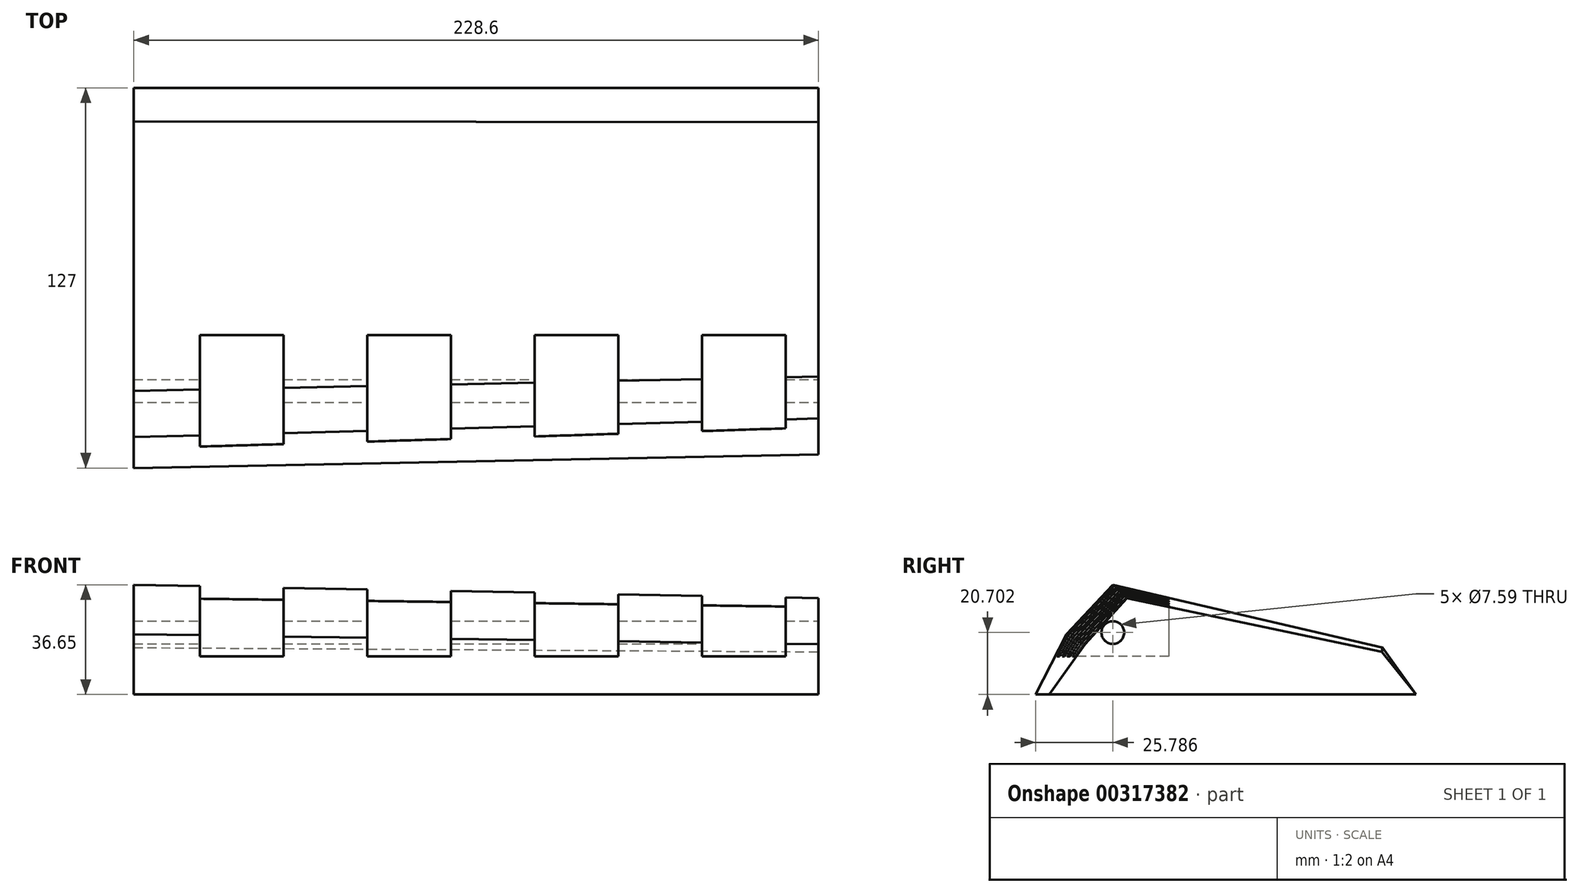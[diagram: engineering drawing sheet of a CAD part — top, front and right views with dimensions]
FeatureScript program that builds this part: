
annotation { "Feature Type Name" : "Feature", "Feature Type Description" : "" }
export const myFeature = defineFeature(function(context is Context, id is Id, definition is map)
    precondition{}
    {
        {
            var Q0;
            Q0=qCreatedBy(makeId("Right.planeOp"),FACE);
            var sketch = newSketch(context, id + "F0", { "sketchPlane" : qUnion([Q0])});
            skLineSegment(sketch, "E0", {"start": v(0, 0) * mm, "end": v(-127, 0) * mm});
            skLineSegment(sketch, "E1", {"start": v(-127, 0) * mm, "end": v(-116.66, 20.14) * mm});
            skLineSegment(sketch, "E2", {"start": v(-116.66, 20.14) * mm, "end": v(-101.27, 36.65) * mm});
            skLineSegment(sketch, "E3", {"start": v(-101.27, 36.65) * mm, "end": v(-11.2, 15.67) * mm});
            skLineSegment(sketch, "E4", {"start": v(-11.2, 15.67) * mm, "end": v(0, 0) * mm});
            skSolve(sketch);
        }
        {
            var Q0;
            Q0=qCreatedBy(makeId("Right.planeOp"),FACE);
            cPlane(context, id + "F1", {"entities" : qUnion([Q0]), "cplaneType" : CPlaneType.OFFSET, "offset" : 228.6 * mm, "width" : 152.4 * mm, "height" : 152.4 * mm});
        }
        {
            var Q0;
            Q0=qCreatedBy(id+"F1.planeOp",FACE);
            var sketch = newSketch(context, id + "F2", { "sketchPlane" : qUnion([Q0])});
            skLineSegment(sketch, "E5", {"start": v(0, 0) * mm, "end": v(-122.48, 0) * mm});
            skLineSegment(sketch, "E6", {"start": v(-122.48, 0) * mm, "end": v(-110.45, 16.79) * mm});
            skLineSegment(sketch, "E7", {"start": v(-110.45, 16.79) * mm, "end": v(-96.46, 32.17) * mm});
            skLineSegment(sketch, "E8", {"start": v(-96.46, 32.17) * mm, "end": v(-11.41, 14.27) * mm});
            skLineSegment(sketch, "E9", {"start": v(-11.41, 14.27) * mm, "end": v(0, 0) * mm});
            skSolve(sketch);
        }
        {
            var Q0;
            Q0=makeQuery(id+"F0.imprint","IMPRINT",FACE,{"disambiguationData":[TD([[makeQuery(id+"F0.imprint","IMPRINT",EDGE,{"derivedFrom":sQuery(id+"F0.wireOp",EDGE,"E0")}),-1.0]])]});
            var Q1;
            Q1=makeQuery(id+"F2.imprint","IMPRINT",FACE,{"disambiguationData":[TD([[makeQuery(id+"F2.imprint","IMPRINT",EDGE,{"derivedFrom":sQuery(id+"F2.wireOp",EDGE,"E5")}),-1.0]])]});
            loft(context, id + "F3", {"sheetProfilesArray" : [{ "sheetProfileEntities" : qUnion([Q0]) }, { "sheetProfileEntities" : qUnion([Q1]) }]});
        }
        {
            var Q0;
            Q0=qCreatedBy(id+"F1.planeOp",FACE);
            var sketch = newSketch(context, id + "F4", { "sketchPlane" : qUnion([Q0])});
            skLineSegment(sketch, "E10", {"start": v(0, 0) * mm, "end": v(-101.21, 0) * mm, "construction": true});
            skLineSegment(sketch, "E11", {"start": v(-101.21, 0) * mm, "end": v(-101.21, 20.7) * mm, "construction": true});
            skCircle(sketch, "E12", {"center": v(-101.21, 20.7) * mm, "radius": 3.8 * mm});
            skLineSegment(sketch, "E13", {"start": v(-105.01, 20.7) * mm, "end": v(-105.01, 0) * mm, "construction": true});
            skLineSegment(sketch, "E14", {"start": v(-97.42, 20.7) * mm, "end": v(-97.42, 0) * mm});
            skSolve(sketch);
        }
        {
            var Q0;
            Q0=makeQuery(id+"F4.imprint","IMPRINT",FACE,{"disambiguationData":[TD([[makeQuery(id+"F4.imprint","IMPRINT",EDGE,{"derivedFrom":sQuery(id+"F4.wireOp",EDGE,"E12")}),1.0]])]});
            extrude(context, id + "F5", {"entities" : qUnion([Q0]), "operationType" : NewBodyOperationType.REMOVE, "oppositeDirection" : true, "depth" : 228.6 * mm});
        }
        {
            var Q0;
            Q0=qCreatedBy(makeId("Top.planeOp"),FACE);
            cPlane(context, id + "F6", {"entities" : qUnion([Q0]), "cplaneType" : CPlaneType.OFFSET, "offset" : 16.92 * mm, "width" : 152.4 * mm, "height" : 152.4 * mm});
        }
        {
            var Q0;
            Q0=qCreatedBy(id+"F6.planeOp",FACE);
            var sketch = newSketch(context, id + "F7", { "sketchPlane" : qUnion([Q0])});
            skLineSegment(sketch, "E15", {"start": v(0, 0) * mm, "end": v(36.07, 0) * mm, "construction": true});
            skLineSegment(sketch, "E16", {"start": v(36.07, 0) * mm, "end": v(91.95, 0) * mm, "construction": true});
            skLineSegment(sketch, "E17", {"start": v(91.95, 0) * mm, "end": v(147.83, 0) * mm, "construction": true});
            skLineSegment(sketch, "E18", {"start": v(147.83, 0) * mm, "end": v(203.7, 0) * mm, "construction": true});
            skLineSegment(sketch, "E19", {"start": v(203.7, 0) * mm, "end": v(203.7, -96.52) * mm});
            skLineSegment(sketch, "E20", {"start": v(203.7, 0) * mm, "end": v(203.7, -106.68) * mm});
            skLineSegment(sketch, "E21", {"start": v(203.7, -96.52) * mm, "end": v(147.83, -96.52) * mm, "construction": true});
            skLineSegment(sketch, "E22", {"start": v(147.83, -96.52) * mm, "end": v(91.95, -96.52) * mm, "construction": true});
            skLineSegment(sketch, "E23", {"start": v(91.95, -96.52) * mm, "end": v(36.07, -96.52) * mm, "construction": true});
            skLineSegment(sketch, "E24", {"start": v(36.07, -96.52) * mm, "end": v(0, -96.52) * mm, "construction": true});
            skLineSegment(sketch, "E25.bottom", {"start": v(50.04, -82.55) * mm, "end": v(22.1, -82.55) * mm});
            skLineSegment(sketch, "E25.top", {"start": v(50.04, -110.49) * mm, "end": v(22.1, -110.49) * mm});
            skLineSegment(sketch, "E25.left", {"start": v(50.04, -82.55) * mm, "end": v(50.04, -110.49) * mm});
            skLineSegment(sketch, "E25.right", {"start": v(22.1, -82.55) * mm, "end": v(22.1, -110.49) * mm});
            skPoint(sketch, "E25.middle", {"position": v(36.07, -96.52) * mm});
            skLineSegment(sketch, "E26.bottom", {"start": v(105.92, -82.55) * mm, "end": v(77.98, -82.55) * mm});
            skLineSegment(sketch, "E26.top", {"start": v(105.92, -110.5) * mm, "end": v(77.98, -110.5) * mm});
            skLineSegment(sketch, "E26.left", {"start": v(105.92, -82.55) * mm, "end": v(105.92, -110.5) * mm});
            skLineSegment(sketch, "E26.right", {"start": v(77.98, -82.55) * mm, "end": v(77.98, -110.5) * mm});
            skPoint(sketch, "E26.middle", {"position": v(91.95, -96.52) * mm});
            skLineSegment(sketch, "E27.bottom", {"start": v(161.8, -82.55) * mm, "end": v(133.86, -82.55) * mm});
            skLineSegment(sketch, "E27.top", {"start": v(161.8, -110.5) * mm, "end": v(133.86, -110.5) * mm});
            skLineSegment(sketch, "E27.left", {"start": v(161.8, -82.55) * mm, "end": v(161.8, -110.5) * mm});
            skLineSegment(sketch, "E27.right", {"start": v(133.86, -82.55) * mm, "end": v(133.86, -110.5) * mm});
            skPoint(sketch, "E27.middle", {"position": v(147.83, -96.52) * mm});
            skLineSegment(sketch, "E28.bottom", {"start": v(189.74, -82.55) * mm, "end": v(217.68, -82.55) * mm});
            skLineSegment(sketch, "E28.top", {"start": v(189.74, -110.5) * mm, "end": v(217.68, -110.5) * mm});
            skLineSegment(sketch, "E28.left", {"start": v(189.74, -82.55) * mm, "end": v(189.74, -110.5) * mm});
            skLineSegment(sketch, "E28.right", {"start": v(217.68, -82.55) * mm, "end": v(217.68, -110.5) * mm});
            skPoint(sketch, "E28.middle", {"position": v(203.7, -96.52) * mm});
            skPoint(sketch, "E28.cornerSnap0", {"position": v(91.95, -82.55) * mm});
            skSolve(sketch);
        }
        {
            var Q0;
            Q0 = qSketchRegion(id + "F7", true);
            extrude(context, id + "F8", {"entities" : qUnion([Q0]), "operationType" : NewBodyOperationType.REMOVE, "depth" : 25.4 * mm});
        }
        {
            var Q0;
            Q0=makeQuery(id+"F8.boolean.opBoolean","COPY",FACE,{"derivedFrom":makeQuery(id+"F8.opExtrude","SWEPT_FACE",FACE,{"disambiguationData":[OSD([sQuery(id+"F7.wireOp",EDGE,"E25.bottom")])]})});
            var sketch = newSketch(context, id + "F9", { "sketchPlane" : qUnion([Q0])});
            skLineSegment(sketch, "E29", {"start": v(22.1, 32) * mm, "end": v(22.1, 16.92) * mm});
            skLineSegment(sketch, "E30", {"start": v(22.1, 16.92) * mm, "end": v(50.04, 16.92) * mm});
            skLineSegment(sketch, "E31", {"start": v(50.04, 16.92) * mm, "end": v(50.04, 31.64) * mm});
            skLineSegment(sketch, "E32", {"start": v(50.04, 31.64) * mm, "end": v(22.1, 32) * mm});
            skSolve(sketch);
        }
        {
            var Q0;
            Q0=makeQuery(id+"F8.boolean.opBoolean","COPY",FACE,{"derivedFrom":makeQuery(id+"F8.opExtrude","SWEPT_FACE",FACE,{"disambiguationData":[OSD([sQuery(id+"F7.wireOp",EDGE,"E26.bottom")])]})});
            var sketch = newSketch(context, id + "F10", { "sketchPlane" : qUnion([Q0])});
            skLineSegment(sketch, "E33", {"start": v(77.98, 31.27) * mm, "end": v(77.98, 16.92) * mm});
            skLineSegment(sketch, "E34", {"start": v(77.98, 16.92) * mm, "end": v(105.92, 16.92) * mm});
            skLineSegment(sketch, "E35", {"start": v(105.92, 16.92) * mm, "end": v(105.92, 30.9) * mm});
            skLineSegment(sketch, "E36", {"start": v(105.92, 30.9) * mm, "end": v(77.98, 31.27) * mm});
            skSolve(sketch);
        }
        {
            var Q0;
            Q0=makeQuery(id+"F8.boolean.opBoolean","COPY",FACE,{"derivedFrom":makeQuery(id+"F8.opExtrude","SWEPT_FACE",FACE,{"disambiguationData":[OSD([sQuery(id+"F7.wireOp",EDGE,"E27.bottom")])]})});
            var sketch = newSketch(context, id + "F11", { "sketchPlane" : qUnion([Q0])});
            skLineSegment(sketch, "E37", {"start": v(133.86, 30.53) * mm, "end": v(133.86, 16.92) * mm});
            skLineSegment(sketch, "E38", {"start": v(133.86, 16.92) * mm, "end": v(161.8, 16.92) * mm});
            skLineSegment(sketch, "E39", {"start": v(161.8, 16.92) * mm, "end": v(161.8, 30.15) * mm});
            skLineSegment(sketch, "E40", {"start": v(161.8, 30.15) * mm, "end": v(133.86, 30.53) * mm});
            skSolve(sketch);
        }
        {
            var Q0;
            Q0=makeQuery(id+"F8.boolean.opBoolean","COPY",FACE,{"derivedFrom":makeQuery(id+"F8.opExtrude","SWEPT_FACE",FACE,{"disambiguationData":[OSD([sQuery(id+"F7.wireOp",EDGE,"E28.bottom")])]})});
            var sketch = newSketch(context, id + "F12", { "sketchPlane" : qUnion([Q0])});
            skLineSegment(sketch, "E41", {"start": v(189.74, 29.77) * mm, "end": v(189.74, 16.92) * mm});
            skLineSegment(sketch, "E42", {"start": v(189.74, 16.92) * mm, "end": v(217.68, 16.92) * mm});
            skLineSegment(sketch, "E43", {"start": v(217.68, 16.92) * mm, "end": v(217.68, 29.4) * mm});
            skLineSegment(sketch, "E44", {"start": v(217.68, 29.4) * mm, "end": v(189.74, 29.77) * mm});
            skSolve(sketch);
        }
        {
            var Q0;
            Q0 = qSketchRegion(id + "F9", true);
            var Q1;
            Q1 = qSketchRegion(id + "F10", true);
            var Q2;
            Q2 = qSketchRegion(id + "F11", true);
            var Q3;
            Q3 = qSketchRegion(id + "F12", true);
            extrude(context, id + "F13", {"entities" : qUnion([Q0, Q1, Q2, Q3]), "operationType" : NewBodyOperationType.REMOVE, "depth" : 609.6 * mm});
        }
        {
            var Q0;
            Q0=qCreatedBy(makeId("Top.planeOp"),FACE);
            cPlane(context, id + "F14", {"entities" : qUnion([Q0]), "cplaneType" : CPlaneType.OFFSET, "offset" : 12.7 * mm, "width" : 152.4 * mm, "height" : 152.4 * mm});
        }
        {
            var Q0;
            Q0=qCreatedBy(id+"F14.planeOp",FACE);
            var sketch = newSketch(context, id + "F15", { "sketchPlane" : qUnion([Q0])});
            skLineSegment(sketch, "E45", {"start": v(0, 0) * mm, "end": v(36.07, 0) * mm, "construction": true});
            skLineSegment(sketch, "E46", {"start": v(36.07, 0) * mm, "end": v(91.95, 0) * mm, "construction": true});
            skPoint(sketch, "E46.endSnap0", {"position": v(18.03, 0) * mm});
            skLineSegment(sketch, "E47", {"start": v(91.95, 0) * mm, "end": v(147.83, 0) * mm, "construction": true});
            skLineSegment(sketch, "E48", {"start": v(147.83, 0) * mm, "end": v(203.7, 0) * mm, "construction": true});
            skLineSegment(sketch, "E49", {"start": v(203.7, 0) * mm, "end": v(203.7, -96.52) * mm, "construction": true});
            skLineSegment(sketch, "E50", {"start": v(203.7, -96.52) * mm, "end": v(147.83, -96.52) * mm, "construction": true});
            skLineSegment(sketch, "E51", {"start": v(147.83, -96.52) * mm, "end": v(91.95, -96.52) * mm, "construction": true});
            skLineSegment(sketch, "E52", {"start": v(91.95, -96.52) * mm, "end": v(36.07, -96.52) * mm, "construction": true});
            skLineSegment(sketch, "E53", {"start": v(36.07, -96.52) * mm, "end": v(0, -96.52) * mm, "construction": true});
            skLineSegment(sketch, "E54.bottom", {"start": v(50.04, -82.55) * mm, "end": v(22.1, -82.55) * mm});
            skLineSegment(sketch, "E54.top", {"start": v(50.04, -110.49) * mm, "end": v(22.1, -110.49) * mm});
            skLineSegment(sketch, "E54.left", {"start": v(50.04, -82.55) * mm, "end": v(50.04, -110.49) * mm});
            skLineSegment(sketch, "E54.right", {"start": v(22.1, -82.55) * mm, "end": v(22.1, -110.49) * mm});
            skPoint(sketch, "E54.middle", {"position": v(36.07, -96.52) * mm});
            skLineSegment(sketch, "E55.bottom", {"start": v(105.92, -82.55) * mm, "end": v(77.98, -82.55) * mm});
            skLineSegment(sketch, "E55.top", {"start": v(105.92, -110.49) * mm, "end": v(77.98, -110.49) * mm});
            skLineSegment(sketch, "E55.left", {"start": v(105.92, -82.55) * mm, "end": v(105.92, -110.49) * mm});
            skLineSegment(sketch, "E55.right", {"start": v(77.98, -82.55) * mm, "end": v(77.98, -110.49) * mm});
            skPoint(sketch, "E55.middle", {"position": v(91.95, -96.52) * mm});
            skLineSegment(sketch, "E56.bottom", {"start": v(161.8, -82.55) * mm, "end": v(133.86, -82.55) * mm});
            skLineSegment(sketch, "E56.top", {"start": v(161.8, -110.49) * mm, "end": v(133.86, -110.49) * mm});
            skLineSegment(sketch, "E56.left", {"start": v(161.8, -82.55) * mm, "end": v(161.8, -110.49) * mm});
            skLineSegment(sketch, "E56.right", {"start": v(133.86, -82.55) * mm, "end": v(133.86, -110.49) * mm});
            skPoint(sketch, "E56.middle", {"position": v(147.83, -96.52) * mm});
            skLineSegment(sketch, "E57.bottom", {"start": v(217.68, -82.55) * mm, "end": v(189.74, -82.55) * mm});
            skLineSegment(sketch, "E57.top", {"start": v(217.68, -110.49) * mm, "end": v(189.74, -110.49) * mm});
            skLineSegment(sketch, "E57.left", {"start": v(217.68, -82.55) * mm, "end": v(217.68, -110.49) * mm});
            skLineSegment(sketch, "E57.right", {"start": v(189.74, -82.55) * mm, "end": v(189.74, -110.49) * mm});
            skPoint(sketch, "E57.middle", {"position": v(203.7, -96.52) * mm});
            skSolve(sketch);
        }
        {
            var Q0;
            Q0 = qSketchRegion(id + "F15", true);
            extrude(context, id + "F16", {"entities" : qUnion([Q0]), "operationType" : NewBodyOperationType.REMOVE, "depth" : 25.4 * mm});
        }
        {
            var Q0;
            Q0=makeQuery(id+"F16.boolean.opBoolean","MERGE",FACE,{"derivedFrom":[makeQuery(id+"F8.boolean.opBoolean","COPY",FACE,{"derivedFrom":makeQuery(id+"F8.opExtrude","SWEPT_FACE",FACE,{"disambiguationData":[OSD([sQuery(id+"F7.wireOp",EDGE,"E25.bottom")])]})}),makeQuery(id+"F16.opExtrude","SWEPT_FACE",FACE,{"disambiguationData":[OSD([sQuery(id+"F15.wireOp",EDGE,"E54.bottom")])]})]});
            var sketch = newSketch(context, id + "F17", { "sketchPlane" : qUnion([Q0])});
            skLineSegment(sketch, "E58", {"start": v(22.1, 32) * mm, "end": v(22.1, 12.7) * mm});
            skLineSegment(sketch, "E59", {"start": v(22.1, 12.7) * mm, "end": v(50.04, 12.7) * mm});
            skLineSegment(sketch, "E60", {"start": v(50.04, 12.7) * mm, "end": v(50.04, 31.64) * mm});
            skLineSegment(sketch, "E61", {"start": v(50.04, 31.64) * mm, "end": v(22.1, 32) * mm});
            skSolve(sketch);
        }
        {
            var Q0;
            Q0=makeQuery(id+"F16.boolean.opBoolean","MERGE",FACE,{"derivedFrom":[makeQuery(id+"F8.boolean.opBoolean","COPY",FACE,{"derivedFrom":makeQuery(id+"F8.opExtrude","SWEPT_FACE",FACE,{"disambiguationData":[OSD([sQuery(id+"F7.wireOp",EDGE,"E26.bottom")])]})}),makeQuery(id+"F16.opExtrude","SWEPT_FACE",FACE,{"disambiguationData":[OSD([sQuery(id+"F15.wireOp",EDGE,"E55.bottom")])]})]});
            var sketch = newSketch(context, id + "F18", { "sketchPlane" : qUnion([Q0])});
            skLineSegment(sketch, "E62", {"start": v(77.98, 31.27) * mm, "end": v(77.98, 12.7) * mm});
            skLineSegment(sketch, "E63", {"start": v(77.98, 12.7) * mm, "end": v(105.92, 12.7) * mm});
            skLineSegment(sketch, "E64", {"start": v(105.92, 12.7) * mm, "end": v(105.92, 30.9) * mm});
            skLineSegment(sketch, "E65", {"start": v(105.92, 30.9) * mm, "end": v(77.98, 31.27) * mm});
            skSolve(sketch);
        }
        {
            var Q0;
            Q0=makeQuery(id+"F16.boolean.opBoolean","MERGE",FACE,{"derivedFrom":[makeQuery(id+"F8.boolean.opBoolean","COPY",FACE,{"derivedFrom":makeQuery(id+"F8.opExtrude","SWEPT_FACE",FACE,{"disambiguationData":[OSD([sQuery(id+"F7.wireOp",EDGE,"E27.bottom")])]})}),makeQuery(id+"F16.opExtrude","SWEPT_FACE",FACE,{"disambiguationData":[OSD([sQuery(id+"F15.wireOp",EDGE,"E56.bottom")])]})]});
            var sketch = newSketch(context, id + "F19", { "sketchPlane" : qUnion([Q0])});
            skLineSegment(sketch, "E66", {"start": v(133.86, 30.53) * mm, "end": v(133.86, 12.7) * mm});
            skLineSegment(sketch, "E67", {"start": v(133.86, 12.7) * mm, "end": v(161.8, 12.7) * mm});
            skLineSegment(sketch, "E68", {"start": v(161.8, 12.7) * mm, "end": v(161.8, 30.15) * mm});
            skLineSegment(sketch, "E69", {"start": v(161.8, 30.15) * mm, "end": v(133.86, 30.53) * mm});
            skSolve(sketch);
        }
        {
            var Q0;
            Q0=makeQuery(id+"F16.boolean.opBoolean","MERGE",FACE,{"derivedFrom":[makeQuery(id+"F8.boolean.opBoolean","COPY",FACE,{"derivedFrom":makeQuery(id+"F8.opExtrude","SWEPT_FACE",FACE,{"disambiguationData":[OSD([sQuery(id+"F7.wireOp",EDGE,"E28.bottom")])]})}),makeQuery(id+"F16.opExtrude","SWEPT_FACE",FACE,{"disambiguationData":[OSD([sQuery(id+"F15.wireOp",EDGE,"E57.bottom")])]})]});
            var sketch = newSketch(context, id + "F20", { "sketchPlane" : qUnion([Q0])});
            skLineSegment(sketch, "E70", {"start": v(189.74, 29.77) * mm, "end": v(189.74, 12.7) * mm});
            skLineSegment(sketch, "E71", {"start": v(189.74, 12.7) * mm, "end": v(217.68, 12.7) * mm});
            skLineSegment(sketch, "E72", {"start": v(217.68, 12.7) * mm, "end": v(217.68, 29.4) * mm});
            skLineSegment(sketch, "E73", {"start": v(217.68, 29.4) * mm, "end": v(189.74, 29.77) * mm});
            skSolve(sketch);
        }
        {
            var Q0;
            Q0=makeQuery(id+"F17.imprint","IMPRINT",FACE,{"disambiguationData":[TD([[makeQuery(id+"F17.imprint","IMPRINT",EDGE,{"derivedFrom":sQuery(id+"F17.wireOp",EDGE,"E58")}),1.0]])]});
            var Q1;
            Q1=makeQuery(id+"F18.imprint","IMPRINT",FACE,{"disambiguationData":[TD([[makeQuery(id+"F18.imprint","IMPRINT",EDGE,{"derivedFrom":sQuery(id+"F18.wireOp",EDGE,"E62")}),1.0]])]});
            var Q2;
            Q2=makeQuery(id+"F19.imprint","IMPRINT",FACE,{"disambiguationData":[TD([[makeQuery(id+"F19.imprint","IMPRINT",EDGE,{"derivedFrom":sQuery(id+"F19.wireOp",EDGE,"E66")}),1.0]])]});
            var Q3;
            Q3=makeQuery(id+"F20.imprint","IMPRINT",FACE,{"disambiguationData":[TD([[makeQuery(id+"F20.imprint","IMPRINT",EDGE,{"derivedFrom":sQuery(id+"F20.wireOp",EDGE,"E70")}),1.0]])]});
            extrude(context, id + "F21", {"entities" : qUnion([Q0, Q1, Q2, Q3]), "operationType" : NewBodyOperationType.REMOVE, "depth" : 50.8 * mm});
        }
    });
